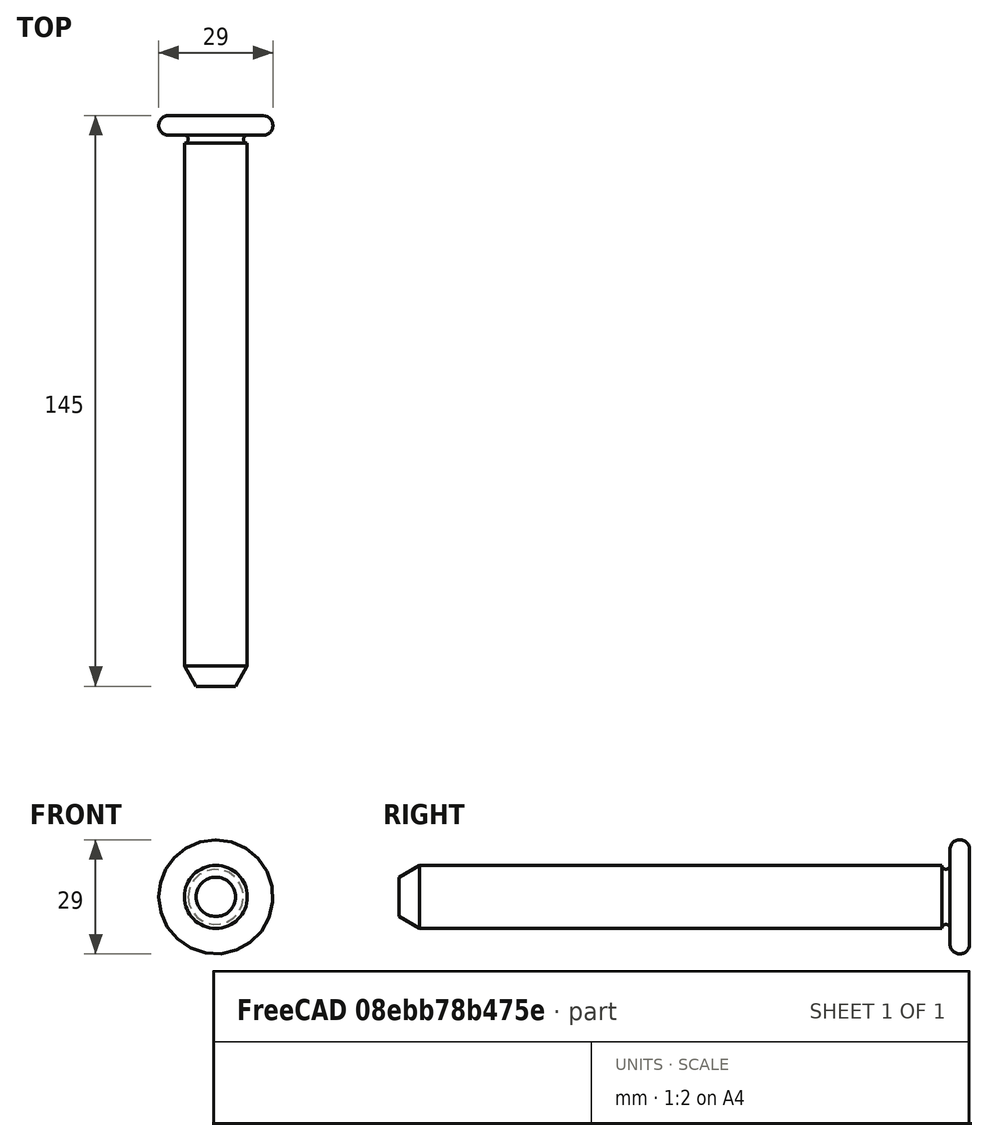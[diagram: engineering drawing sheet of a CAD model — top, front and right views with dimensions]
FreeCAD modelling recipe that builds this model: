
FCSTD DOCUMENT  (FreeCAD 0.18R4 (GitTag))
Label: door-hinge-pin
License: All rights reserved
LicenseURL: http://en.wikipedia.org/wiki/All_rights_reserved
objects: Sketcher::SketchObject×1, PartDesign::Revolution×1, PartDesign::Body×1
note: 4 computed .brp shape members not serialized (recipe doc carries the construction recipe); baked Part::Feature solids carry a one-line shape summary decoded from their .brp

FEATURE [Sketcher::SketchObject] Sketch
  MapMode = 5
  Support = -> [XY_Plane]
  sketch-geometry (8):
    g0: ArcOfCircle CenterX=-12 CenterY=-2.5 CenterZ=0 NormalX=0 NormalY=0 NormalZ=1 AngleXU=0 Radius=2.5 StartAngle=1.5708 EndAngle=4.71239
    g1: LineSegment StartX=-12 StartY=0 StartZ=0 EndX=0 EndY=0 EndZ=0
    g2: LineSegment StartX=-12 StartY=-5 StartZ=0 EndX=-8 EndY=-5 EndZ=0
    g3: ArcOfCircle CenterX=-8 CenterY=-6 CenterZ=0 NormalX=0 NormalY=0 NormalZ=1 AngleXU=0 Radius=1 StartAngle=4.71239 EndAngle=7.85398
    g4: LineSegment StartX=-8 StartY=-7 StartZ=0 EndX=-8 EndY=-139.804 EndZ=0
    g5: LineSegment StartX=-8 StartY=-139.804 StartZ=0 EndX=-5 EndY=-145 EndZ=0
    g6: LineSegment StartX=-5 StartY=-145 StartZ=0 EndX=0 EndY=-145 EndZ=0
    g7: LineSegment StartX=0 StartY=0 StartZ=0 EndX=0 EndY=-145 EndZ=0
  constraints (25):
    c: Coincident(g1,g0)
    c: Coincident(g1,g-1)
    c: Horizontal(g1)
    c: Coincident(g2,g0)
    c: Horizontal(g2)
    c: Coincident(g3,g2)
    c: Coincident(g4,g3)
    c: Vertical(g4)
    c: Coincident(g5,g4)
    c: Coincident(g6,g5)
    c: PointOnObject(g6,g-2)
    c: Radius(g0) = 2.5
    c: Radius(g3) = 1
    c: DistanceX(g1,g1) = 12
    c: DistanceX(g3,g1) = 8
    c: DistanceX(g2,g1) = 8
    c: DistanceY(g3,g2) = 2
    c: DistanceX(g6,g6) = 5
    c: DistanceY(g6,g1) = 145
    c: Horizontal(g6)
    c: DistanceY(g5,g5) = 5.196
    c: Coincident(g7,g1)
    c: Coincident(g7,g6)
    c: Tangent(g2,g0)
    c: Tangent(g1,g0)
FEATURE [PartDesign::Revolution] Revolution
  Angle = 360
  Axis = (1e-16,1,-1e-16)
  Base = (0,0,0)
  Profile = -> Sketch
  ReferenceAxis = -> Y_Axis
  Refine = true
FEATURE [PartDesign::Body] Body
  Group = -> [Sketch,Revolution]
  Origin = -> Origin
  Tip = -> Revolution
